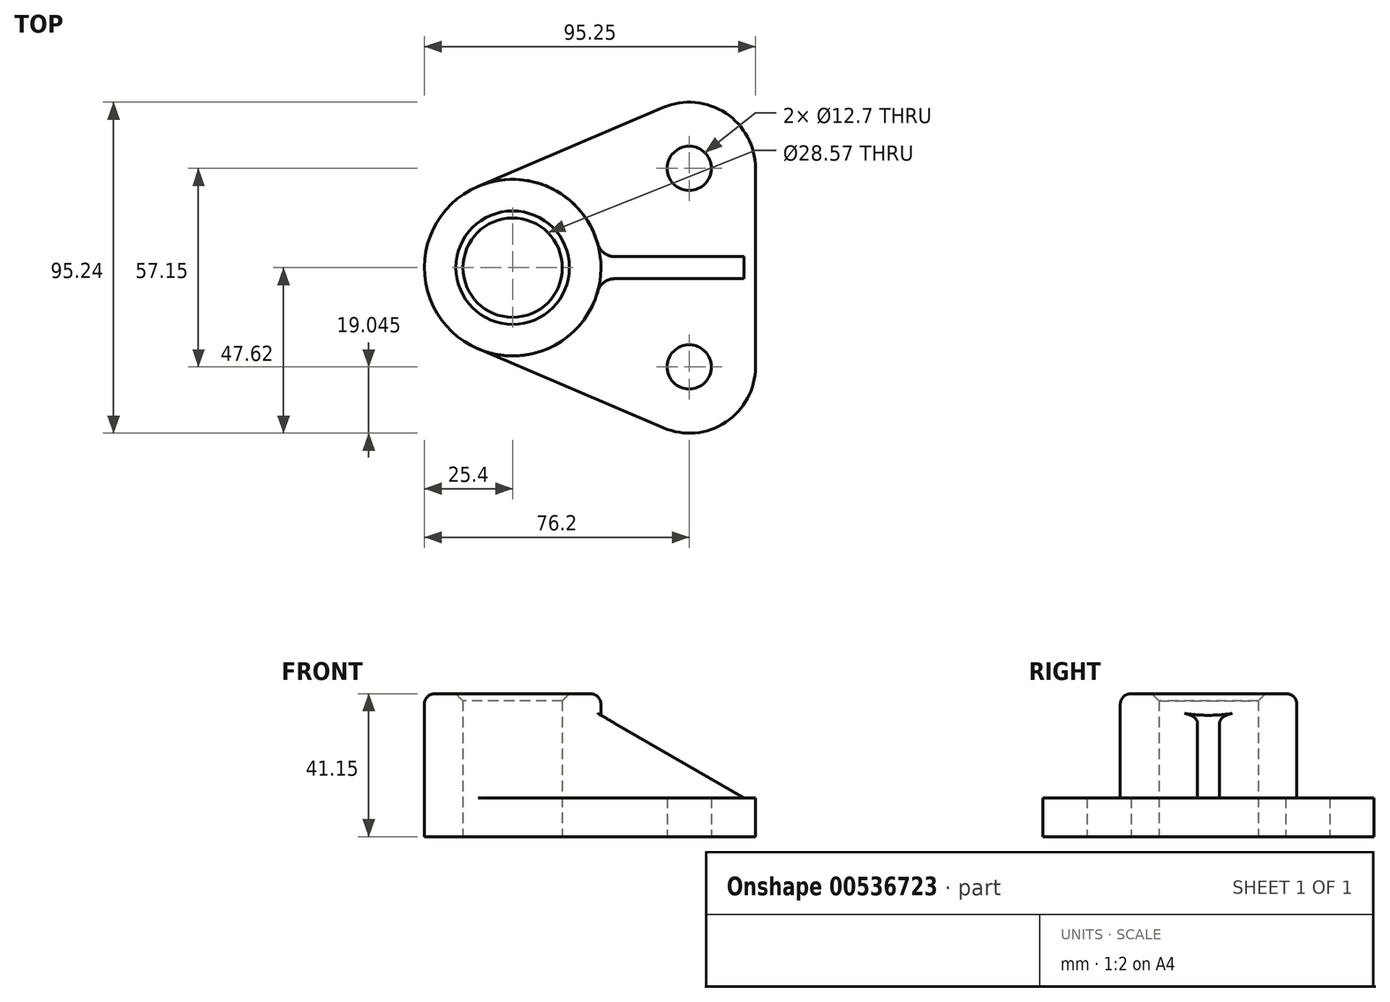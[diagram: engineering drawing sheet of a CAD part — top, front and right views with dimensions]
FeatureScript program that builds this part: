
annotation { "Feature Type Name" : "Feature", "Feature Type Description" : "" }
export const myFeature = defineFeature(function(context is Context, id is Id, definition is map)
    precondition{}
    {
        {
            var Q0;
            Q0=qCreatedBy(makeId("Top.planeOp"),FACE);
            var sketch = newSketch(context, id + "F0", { "sketchPlane" : qUnion([Q0])});
            skLineSegment(sketch, "E0", {"start": v(-101.4, 0) * mm, "end": v(116.06, 0) * mm, "construction": true});
            skCircle(sketch, "E1", {"center": v(0, 0) * mm, "radius": 14.29 * mm});
            skCircle(sketch, "E2", {"center": v(0, 0) * mm, "radius": 25.4 * mm});
            skCircle(sketch, "E3", {"center": v(50.8, -28.58) * mm, "radius": 6.35 * mm});
            skArc(sketch, "E4", {"start": v(43.33, -46.1) * mm, "mid": v(61.3, -44.47) * mm, "end": v(69.85, -28.57) * mm});
            skCircle(sketch, "E5", {"center": v(50.8, 28.58) * mm, "radius": 6.35 * mm});
            skArc(sketch, "E6", {"start": v(69.85, 28.58) * mm, "mid": v(61.3, 44.47) * mm, "end": v(43.33, 46.1) * mm});
            skLineSegment(sketch, "E7", {"start": v(69.85, 28.58) * mm, "end": v(69.85, -28.57) * mm});
            skLineSegment(sketch, "E8", {"start": v(-9.97, 23.36) * mm, "end": v(43.33, 46.1) * mm});
            skLineSegment(sketch, "E9", {"start": v(-9.97, -23.36) * mm, "end": v(43.33, -46.1) * mm});
            skSolve(sketch);
        }
        {
            var Q0;
            Q0=makeQuery(id+"F0.imprint","IMPRINT",FACE,{"disambiguationData":[TD([[makeQuery(id+"F0.imprint","IMPRINT",EDGE,{"derivedFrom":sQuery(id+"F0.wireOp",EDGE,"E1")}),-1.0]])]});
            extrude(context, id + "F1", {"entities" : qUnion([Q0]), "depth" : 41.15 * mm, "offsetDistance" : 25.4 * mm});
        }
        {
            var Q0;
            Q0=makeQuery(id+"F0.imprint","IMPRINT",FACE,{"disambiguationData":[TD([[makeQuery(id+"F0.imprint","IMPRINT",EDGE,{"derivedFrom":sQuery(id+"F0.wireOp",EDGE,"E3")}),-1.0]])]});
            extrude(context, id + "F2", {"entities" : qUnion([Q0]), "operationType" : NewBodyOperationType.ADD, "depth" : 11.18 * mm, "offsetDistance" : 25.4 * mm});
        }
        {
            var Q0;
            Q0=qCreatedBy(makeId("Front.planeOp"),FACE);
            var sketch = newSketch(context, id + "F3", { "sketchPlane" : qUnion([Q0])});
            skLineSegment(sketch, "E10", {"start": v(22.1, 36.84) * mm, "end": v(22.1, 11.18) * mm});
            skLineSegment(sketch, "E11", {"start": v(22.1, 11.18) * mm, "end": v(66.55, 11.18) * mm});
            skLineSegment(sketch, "E12", {"start": v(66.55, 11.18) * mm, "end": v(22.1, 36.84) * mm});
            skSolve(sketch);
        }
        {
            var Q0;
            Q0=makeQuery(id+"F3.imprint","IMPRINT",FACE,{"disambiguationData":[TD([[makeQuery(id+"F3.imprint","IMPRINT",EDGE,{"derivedFrom":sQuery(id+"F3.wireOp",EDGE,"E10")}),1.0]])]});
            extrude(context, id + "F4", {"entities" : qUnion([Q0]), "operationType" : NewBodyOperationType.ADD, "endBound" : BoundingType.SYMMETRIC, "depth" : 6.35 * mm, "offsetDistance" : 25.4 * mm});
        }
        {
            var Q0;
            Q0=makeQuery(id+"F1.opExtrude","CAP_EDGE",EDGE,{"disambiguationData":[OSD([sQuery(id+"F0.wireOp",EDGE,"E2")])],"isStart":false});
            fillet(context, id + "F5", {"entities" : qUnion([Q0]), "radius" : 3.05 * mm, "tangentPropagation" : true, "allowEdgeOverflow" : false});
        }
        {
            var Q0;
            Q0=makeQuery(id+"F4.opExtrude","CAP_EDGE",EDGE,{"disambiguationData":[OSD([sQuery(id+"F3.wireOp",EDGE,"E11")])],"isStart":true});
            var Q1;
            Q1=makeQuery(id+"F4.opExtrude","CAP_EDGE",EDGE,{"disambiguationData":[OSD([sQuery(id+"F3.wireOp",EDGE,"E11")])],"isStart":false});
            var Q2;
            {var subQ0=sQuery(id+"F0.wireOp",EDGE,"E2");var subQ1=sQuery(id+"F0.wireOp",EDGE,"E8");Q2=makeQuery(id+"F4.boolean.opBoolean","SPLIT",EDGE,{"disambiguationData":[TD([makeQuery(id+"F2.opExtrude","SWEPT_FACE",FACE,{"disambiguationData":[OSD([subQ1])]})])],"derivedFrom":makeQuery(id+"F2.opExtrude","CAP_EDGE",EDGE,{"disambiguationData":[OSD([subQ0])],"isStart":false})});}
            var Q3;
            {var subQ0=sQuery(id+"F0.wireOp",EDGE,"E2");var subQ1=sQuery(id+"F0.wireOp",EDGE,"E9");Q3=makeQuery(id+"F4.boolean.opBoolean","SPLIT",EDGE,{"disambiguationData":[TD([makeQuery(id+"F2.opExtrude","SWEPT_FACE",FACE,{"disambiguationData":[OSD([subQ1])]})])],"derivedFrom":makeQuery(id+"F2.opExtrude","CAP_EDGE",EDGE,{"disambiguationData":[OSD([subQ0])],"isStart":false})});}
            var Q4;
            Q4=makeQuery(id+"F4.boolean.opBoolean","INTERSECT",EDGE,{"derivedFrom":[makeQuery(id+"F1.opExtrude","SWEPT_FACE",FACE,{"disambiguationData":[OSD([sQuery(id+"F0.wireOp",EDGE,"E2")])]}),makeQuery(id+"F4.opExtrude","CAP_FACE",FACE,{"disambiguationData":[OSD([sQuery(id+"F3.wireOp",EDGE,"E10"),sQuery(id+"F3.wireOp",EDGE,"E11"),sQuery(id+"F3.wireOp",EDGE,"E12")])],"isStart":false})]});
            var Q5;
            Q5=makeQuery(id+"F4.boolean.opBoolean","INTERSECT",EDGE,{"derivedFrom":[makeQuery(id+"F1.opExtrude","SWEPT_FACE",FACE,{"disambiguationData":[OSD([sQuery(id+"F0.wireOp",EDGE,"E2")])]}),makeQuery(id+"F4.opExtrude","CAP_FACE",FACE,{"disambiguationData":[OSD([sQuery(id+"F3.wireOp",EDGE,"E10"),sQuery(id+"F3.wireOp",EDGE,"E11"),sQuery(id+"F3.wireOp",EDGE,"E12")])],"isStart":true})]});
            fillet(context, id + "F6", {"entities" : qUnion([Q0, Q1, Q2, Q3, Q4, Q5]), "radius" : 5.08 * mm, "tangentPropagation" : true, "allowEdgeOverflow" : false});
        }
        {
            var Q0;
            Q0=makeQuery(id+"F1.opExtrude","CAP_EDGE",EDGE,{"disambiguationData":[OSD([sQuery(id+"F0.wireOp",EDGE,"E1")])],"isStart":false});
            chamfer(context, id + "F7", {"entities" : qUnion([Q0]), "width" : 2.03 * mm, "tangentPropagation" : true});
        }
    });
